# Revit family: oventrop_aktor-m-2p_1012710-11rfa
name_source: partatom
category: Силовые электроприборы
revit_build: Autodesk Revit 2017 (Build: 20160225_1515(x64)
units: mm (PartAtom-declared; Revit-internal decimal feet)

## family parameters
Заголовок OmniClass = Electric Motors
Номер OmniClass = 23.80.10.21
Общий = Да
Основа = Грань
При загрузке вырезать с полостями = Нет
Размер круглого соединителя = Использовать радиус
Сохранять ориентацию аннотаций = Нет
Тип детали = Нормальный
Точка расчета площади = Нет

## types (2) — shared parameters
Ambient Temperature = 0 °C up to +60 °C, not condensing
Connecting Cable = 3-core cable, 1.5 m long
Custom = Нет
Drive = two point (on/off)
EMCS Version = 2.0
ETIM Article Class = EC011290
Family Version = 10.13
Floating Time = about 3 s
Grey = Color RGB 100-100-100
Height = 83 мм
IFCExportAs = IfcActuatorType
IFCExportType = ELECTRICACTUATOR
Length = 81 мм
MEPcontent Class = ACTUATOR
Manufacturer URL = http://www.oventrop.com
Max. Fluid Temperature = 100°C
Max. Piston Stroke = 6.5 mm
Operating Power = > 90 N
Parallel Working = max. of 5 actuators
Power Consumption = 1.8 W during operation, 0.5 W stroke in final position
Product Line = Oventrop
Protection = IP 54
Protective System = II according to EN 60730
Revit Version = 2014
White = Color RGB 245-245-245
Width = 56 мм
Изготовитель = Oventrop
Отметка по умолчанию = 1219.2 мм

## per-type parameters (varying)
| type | Article Description | GTIN | Input Current Control Signal | Manufacturer Art. No. | URL | Voltage | Описание |
| 2710 | Electromotive actuator Aktor M 2P H, 230 V, two point | 4026755332285 | < 10 mA | 1012710 | http://file-system.ru | 230 В | Electromotive actuator Aktor M 2P H, 230 V, two point |
| 2711 | Electromotive actuator  Aktor M 2P L, 24 V, two point | 4026755372182 | 1 mA | 1012711 | www.stabiplan.com | 24 В | Electromotive actuator  Aktor M 2P L, 24 V, two point |

note: column(s) folded — value = type name in every type: Article Type, Группа модели

## geometry (parser evidence)
native form markers: Sweep x2
no freeform markers — native parametric forms only
